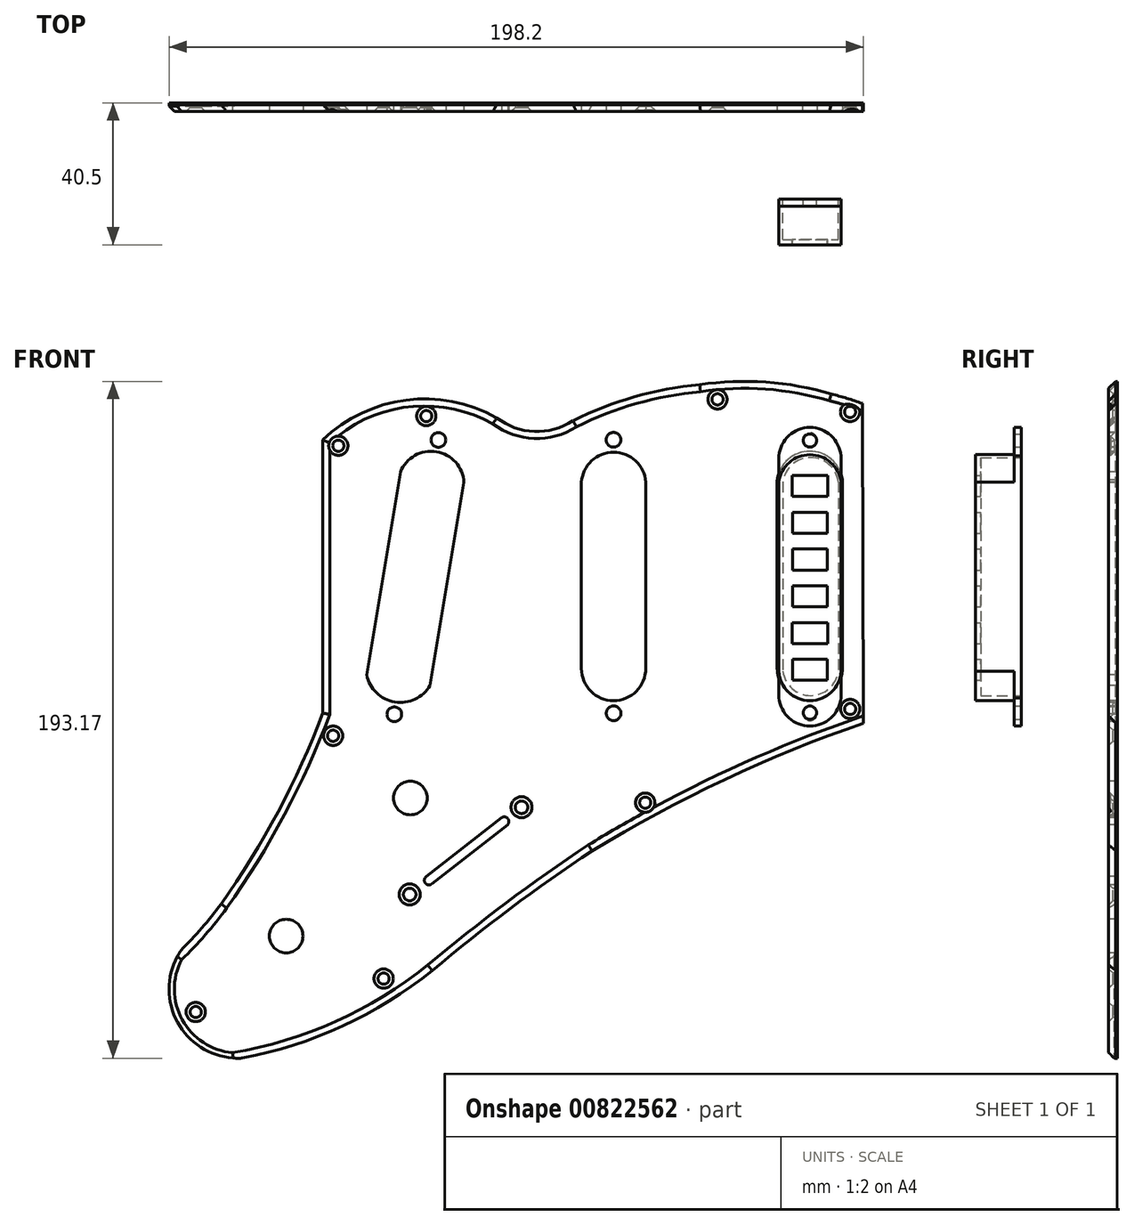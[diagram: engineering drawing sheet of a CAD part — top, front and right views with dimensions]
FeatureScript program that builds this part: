
annotation { "Feature Type Name" : "Feature", "Feature Type Description" : "" }
export const myFeature = defineFeature(function(context is Context, id is Id, definition is map)
    precondition{}
    {
        {
            var Q0;
            Q0=qCreatedBy(makeId("Front.planeOp"),FACE);
            var sketch = newSketch(context, id + "F0", { "sketchPlane" : qUnion([Q0])});
            skLineSegment(sketch, "E0", {"start": v(-59.34, 29.83) * mm, "end": v(-68.97, -28.02) * mm});
            skLineSegment(sketch, "E1", {"start": v(-41.2, 26.83) * mm, "end": v(-50.86, -31.04) * mm});
            skArc(sketch, "E2", {"start": v(-41.2, 26.83) * mm, "mid": v(-49.06, 35.63) * mm, "end": v(-59.34, 29.83) * mm});
            skArc(sketch, "E3", {"start": v(-68.97, -28.02) * mm, "mid": v(-60.95, -35.78) * mm, "end": v(-50.86, -31.04) * mm});
            skLineSegment(sketch, "E4", {"start": v(-7.67, 26.91) * mm, "end": v(-7.67, -26.25) * mm});
            skLineSegment(sketch, "E5", {"start": v(10.69, 26.94) * mm, "end": v(10.69, -26.24) * mm});
            skArc(sketch, "E6", {"start": v(10.69, 26.94) * mm, "mid": v(1.5, 35.5) * mm, "end": v(-7.67, 26.91) * mm});
            skArc(sketch, "E7", {"start": v(-7.67, -26.25) * mm, "mid": v(1.52, -35.42) * mm, "end": v(10.69, -26.24) * mm});
            skLineSegment(sketch, "E8", {"start": v(48.21, 27.6) * mm, "end": v(48.21, -26.25) * mm});
            skLineSegment(sketch, "E9", {"start": v(66.82, 27.62) * mm, "end": v(66.82, -26.21) * mm});
            skArc(sketch, "E10", {"start": v(66.82, 27.62) * mm, "mid": v(57.5, 35.79) * mm, "end": v(48.21, 27.6) * mm});
            skArc(sketch, "E11", {"start": v(48.21, -26.25) * mm, "mid": v(57.54, -35.51) * mm, "end": v(66.82, -26.21) * mm});
            skLineSegment(sketch, "E12", {"start": v(-81.5, 39) * mm, "end": v(-81.5, -38.96) * mm});
            skPoint(sketch, "E13", {"position": v(-31.85, 45.3) * mm});
            skPoint(sketch, "E14", {"position": v(-10.07, 44.47) * mm});
            skArc(sketch, "E15", {"start": v(-31.85, 45.3) * mm, "mid": v(-57.72, 50.37) * mm, "end": v(-81.5, 39) * mm});
            skArc(sketch, "E16", {"start": v(-31.85, 45.3) * mm, "mid": v(-21.1, 41.42) * mm, "end": v(-10.07, 44.47) * mm});
            skLineSegment(sketch, "E17", {"start": v(-81.5, 0) * mm, "end": v(-157.06, 0) * mm, "construction": true});
            skPoint(sketch, "E17.startSnap0", {"position": v(-81.5, 0.02) * mm});
            skLineSegment(sketch, "E18", {"start": v(-81.5, 0) * mm, "end": v(-144.5, 0) * mm, "construction": true});
            skLineSegment(sketch, "E19", {"start": v(-144.5, 0) * mm, "end": v(-144.5, -173.82) * mm, "construction": true});
            skLineSegment(sketch, "E20", {"start": v(-60.95, -39) * mm, "end": v(-60.95, -151.87) * mm, "construction": true});
            skPoint(sketch, "E20.startSnap0", {"position": v(-60.95, -35.78) * mm});
            skLineSegment(sketch, "E21", {"start": v(-60.95, -39) * mm, "end": v(-60.95, -133) * mm, "construction": true});
            skLineSegment(sketch, "E22", {"start": v(-60.95, -133) * mm, "end": v(-144.5, -133) * mm, "construction": true});
            skLineSegment(sketch, "E23", {"start": v(-60.95, -39) * mm, "end": v(-60.95, -120) * mm, "construction": true});
            skLineSegment(sketch, "E24", {"start": v(1.52, -39.01) * mm, "end": v(1.52, -84.86) * mm, "construction": true});
            skPoint(sketch, "E24.startSnap0", {"position": v(1.52, -35.42) * mm});
            skArc(sketch, "E25", {"start": v(72.84, -41.86) * mm, "mid": v(33.11, -57.95) * mm, "end": v(-4.63, -78.27) * mm});
            skLineSegment(sketch, "E26", {"start": v(-144.5, -120.92) * mm, "end": v(-81.56, -44.3) * mm, "construction": true});
            skArc(sketch, "E27", {"start": v(-4.63, -78.27) * mm, "mid": v(-27.92, -94.7) * mm, "end": v(-50.26, -112.42) * mm});
            skPoint(sketch, "E28", {"position": v(57.54, -39.01) * mm});
            skPoint(sketch, "E28.positionSnap0", {"position": v(57.54, -35.51) * mm});
            skPoint(sketch, "E29", {"position": v(57.52, 38.98) * mm});
            skPoint(sketch, "E30", {"position": v(1.5, 39.04) * mm});
            skPoint(sketch, "E31", {"position": v(-48.5, 39) * mm});
            skArc(sketch, "E32", {"start": v(72.51, 49.43) * mm, "mid": v(68.1, 50.89) * mm, "end": v(63.62, 52.12) * mm});
            skPoint(sketch, "E33.orphan", {"position": v(36.12, 48.4) * mm});
            skArc(sketch, "E34", {"start": v(26.07, 54.77) * mm, "mid": v(7.52, 51.3) * mm, "end": v(-10.07, 44.47) * mm});
            skPoint(sketch, "E34.startSnap0", {"position": v(38.43, 54.8) * mm});
            skArc(sketch, "E35", {"start": v(63.62, 52.12) * mm, "mid": v(45, 55.5) * mm, "end": v(26.07, 54.77) * mm});
            skPoint(sketch, "E36.orphan", {"position": v(44.43, 54.8) * mm});
            skPoint(sketch, "E37.center.orphan", {"position": v(-117.3, -126.97) * mm});
            skPoint(sketch, "E38.orphan", {"position": v(-117.3, -133) * mm});
            skLineSegment(sketch, "E39", {"start": v(72.51, 49.43) * mm, "end": v(72.84, -41.86) * mm});
            skPoint(sketch, "E40.center.orphan", {"position": v(72.84, 39.25) * mm});
            skPoint(sketch, "E41.endSnap0", {"position": v(-102.73, -133) * mm});
            skPoint(sketch, "E42.orphan", {"position": v(-102.73, -132.29) * mm});
            skArc(sketch, "E43", {"start": v(-110.53, -93.4) * mm, "mid": v(-94.27, -67.11) * mm, "end": v(-81.5, -38.96) * mm});
            skArc(sketch, "E44", {"start": v(-121.98, -106.7) * mm, "mid": v(-116, -100.28) * mm, "end": v(-110.53, -93.4) * mm});
            skArc(sketch, "E45.trimOffspring", {"start": v(-121.98, -106.7) * mm, "mid": v(-122.77, -127.52) * mm, "end": v(-104.44, -137.41) * mm});
            skArc(sketch, "E46", {"start": v(-104.44, -137.41) * mm, "mid": v(-75.8, -128.26) * mm, "end": v(-50.26, -112.42) * mm});
            skSolve(sketch);
        }
        {
            var Q0;
            Q0=makeQuery(id+"F0.imprint","IMPRINT",FACE,{"disambiguationData":[TD([[makeQuery(id+"F0.imprint","IMPRINT",EDGE,{"derivedFrom":sQuery(id+"F0.wireOp",EDGE,"E0")}),-1.0]])]});
            extrude(context, id + "F1", {"entities" : qUnion([Q0]), "oppositeDirection" : true, "depth" : 2.5 * mm, "offsetDistance" : 25 * mm});
        }
        {
            var Q0;
            Q0=qCreatedBy(makeId("Front.planeOp"),FACE);
            var sketch = newSketch(context, id + "F2", { "sketchPlane" : qUnion([Q0])});
            skLineSegment(sketch, "E47", {"start": v(-61.06, -39.3) * mm, "end": v(-61.06, -69.3) * mm, "construction": true});
            skPoint(sketch, "E48", {"position": v(-25.45, -64.9) * mm});
            skLineSegment(sketch, "E49", {"start": v(-29.58, -68.14) * mm, "end": v(-52.08, -85.73) * mm, "construction": true});
            skLineSegment(sketch, "E50", {"start": v(-41.4, -77.38) * mm, "end": v(-39.8, -79.43) * mm, "construction": true});
            skLineSegment(sketch, "E51", {"start": v(-41.4, -77.38) * mm, "end": v(-29.58, -68.14) * mm, "construction": true});
            skLineSegment(sketch, "E52", {"start": v(-39.8, -79.43) * mm, "end": v(-28.73, -70.77) * mm});
            skLineSegment(sketch, "E53", {"start": v(-39.8, -79.43) * mm, "end": v(-50.4, -87.72) * mm});
            skLineSegment(sketch, "E54", {"start": v(-41.4, -77.38) * mm, "end": v(-43, -75.33) * mm, "construction": true});
            skArc(sketch, "E55", {"start": v(-28.73, -70.77) * mm, "mid": v(-28.69, -69.04) * mm, "end": v(-30.4, -68.78) * mm});
            skArc(sketch, "E56", {"start": v(-51.92, -85.6) * mm, "mid": v(-52.26, -87.45) * mm, "end": v(-50.4, -87.72) * mm});
            skLineSegment(sketch, "E57", {"start": v(-51.92, -85.6) * mm, "end": v(-30.4, -68.78) * mm});
            skPoint(sketch, "E58", {"position": v(-57.35, -89.85) * mm});
            skPoint(sketch, "E59.end.orphan", {"position": v(0, -69.3) * mm});
            skPoint(sketch, "E60", {"position": v(-24.76, -65.83) * mm});
            skPoint(sketch, "E61", {"position": v(-56.69, -90.72) * mm});
            skSolve(sketch);
        }
        {
            var Q0;
            Q0=makeQuery(id+"F2.imprint","IMPRINT",FACE,{"disambiguationData":[TD([[makeQuery(id+"F2.imprint","IMPRINT",EDGE,{"derivedFrom":sQuery(id+"F2.wireOp",EDGE,"E52")}),1.0]])]});
            extrude(context, id + "F3", {"entities" : qUnion([Q0]), "operationType" : NewBodyOperationType.REMOVE, "oppositeDirection" : true, "depth" : 25 * mm, "offsetDistance" : 25 * mm});
        }
        {
            var Q0;
            Q0=qCreatedBy(makeId("Front.planeOp"),FACE);
            var sketch = newSketch(context, id + "F4", { "sketchPlane" : qUnion([Q0])});
            skLineSegment(sketch, "E62", {"start": v(-56.5, -39.58) * mm, "end": v(-56.5, -63.18) * mm, "construction": true});
            skLineSegment(sketch, "E63", {"start": v(-56.5, -63.18) * mm, "end": v(-91.93, -102.6) * mm, "construction": true});
            skSolve(sketch);
        }
        {
            var Q0;
            Q0=makeQuery(id+"F1.opExtrude","CAP_EDGE",EDGE,{"disambiguationData":[OSD([sQuery(id+"F0.wireOp",EDGE,"E27")])],"isStart":true});
            var Q1;
            Q1=makeQuery(id+"F1.opExtrude","CAP_EDGE",EDGE,{"disambiguationData":[OSD([sQuery(id+"F0.wireOp",EDGE,"3f65a524-5e08-4ee6-b38e-8508104c908b")])],"isStart":true});
            var Q2;
            Q2=makeQuery(id+"F1.opExtrude","CAP_EDGE",EDGE,{"disambiguationData":[OSD([sQuery(id+"F0.wireOp",EDGE,"6fd70a0b-cebc-4114-900a-990a1ef0163f")])],"isStart":true});
            var Q3;
            Q3=makeQuery(id+"F1.opExtrude","CAP_EDGE",EDGE,{"disambiguationData":[OSD([sQuery(id+"F0.wireOp",EDGE,"E37")])],"isStart":true});
            var Q4;
            Q4=makeQuery(id+"F1.opExtrude","CAP_EDGE",EDGE,{"disambiguationData":[OSD([sQuery(id+"F0.wireOp",EDGE,"2909704d-9c86-453f-addf-d0fc15c74224")])],"isStart":true});
            var Q5;
            Q5=makeQuery(id+"F1.opExtrude","CAP_EDGE",EDGE,{"disambiguationData":[OSD([sQuery(id+"F0.wireOp",EDGE,"E12")])],"isStart":true});
            var Q6;
            Q6=makeQuery(id+"F1.opExtrude","CAP_EDGE",EDGE,{"disambiguationData":[OSD([sQuery(id+"F0.wireOp",EDGE,"E16")])],"isStart":true});
            var Q7;
            Q7=makeQuery(id+"F1.opExtrude","CAP_EDGE",EDGE,{"disambiguationData":[OSD([sQuery(id+"F0.wireOp",EDGE,"3eeeb8b3-c194-4a8c-ba39-98cc53ac4797")])],"isStart":true});
            var Q8;
            Q8=makeQuery(id+"F1.opExtrude","CAP_EDGE",EDGE,{"disambiguationData":[OSD([sQuery(id+"F0.wireOp",EDGE,"E15")])],"isStart":true});
            var Q9;
            Q9=makeQuery(id+"F1.opExtrude","CAP_EDGE",EDGE,{"disambiguationData":[OSD([sQuery(id+"F0.wireOp",EDGE,"koqNDL3g-AHsU-HZZl-Ag6O-zdApHysT2NHa")])],"isStart":true});
            chamfer(context, id + "F5", {"entities" : qUnion([Q0, Q1, Q2, Q3, Q4, Q5, Q6, Q7, Q8, Q9]), "width" : 2 * mm, "tangentPropagation" : true});
        }
        {
            var Q0;
            Q0=qCreatedBy(makeId("Front.planeOp"),FACE);
            var sketch = newSketch(context, id + "F6", { "sketchPlane" : qUnion([Q0])});
            skPoint(sketch, "E64", {"position": v(-117.76, -124.26) * mm});
            skPoint(sketch, "E65", {"position": v(-78.53, -45.43) * mm});
            skPoint(sketch, "E66", {"position": v(-77.05, 37.34) * mm});
            skPoint(sketch, "E67", {"position": v(-51.95, 45.82) * mm});
            skPoint(sketch, "E68", {"position": v(31.17, 50.59) * mm});
            skPoint(sketch, "E69", {"position": v(69, 47) * mm});
            skPoint(sketch, "E70", {"position": v(69.05, -37.78) * mm});
            skPoint(sketch, "E71", {"position": v(10.55, -64.5) * mm});
            skPoint(sketch, "E72", {"position": v(-64.12, -114.73) * mm});
            skSolve(sketch);
        }
        {
            var Q0;
            Q0=sQuery(id+"F6.wireOp",VERTEX,"E71");
            var Q1;
            Q1=sQuery(id+"F6.wireOp",VERTEX,"E72");
            var Q2;
            Q2=sQuery(id+"F6.wireOp",VERTEX,"E64");
            var Q3;
            Q3=sQuery(id+"F6.wireOp",VERTEX,"E65");
            var Q4;
            Q4=sQuery(id+"F6.wireOp",VERTEX,"E66");
            var Q5;
            Q5=sQuery(id+"F6.wireOp",VERTEX,"E67");
            var Q6;
            Q6=sQuery(id+"F6.wireOp",VERTEX,"E68");
            var Q7;
            Q7=sQuery(id+"F6.wireOp",VERTEX,"E69");
            var Q8;
            Q8=sQuery(id+"F6.wireOp",VERTEX,"E70");
            var Q9;
            Q9=makeQuery(id+"F1.opExtrude","SWEPT_BODY",BODY,{"disambiguationData":[OSD([sQuery(id+"F0.wireOp",EDGE,"E0"),sQuery(id+"F0.wireOp",EDGE,"E1"),sQuery(id+"F0.wireOp",EDGE,"E2"),sQuery(id+"F0.wireOp",EDGE,"E3"),sQuery(id+"F0.wireOp",EDGE,"E4"),sQuery(id+"F0.wireOp",EDGE,"E5"),sQuery(id+"F0.wireOp",EDGE,"E6"),sQuery(id+"F0.wireOp",EDGE,"E7"),sQuery(id+"F0.wireOp",EDGE,"E8"),sQuery(id+"F0.wireOp",EDGE,"E9"),sQuery(id+"F0.wireOp",EDGE,"E10"),sQuery(id+"F0.wireOp",EDGE,"E11"),sQuery(id+"F0.wireOp",EDGE,"koqNDL3g-AHsU-HZZl-Ag6O-zdApHysT2NHa"),sQuery(id+"F0.wireOp",EDGE,"E12"),sQuery(id+"F0.wireOp",EDGE,"E15"),sQuery(id+"F0.wireOp",EDGE,"E16"),sQuery(id+"F0.wireOp",EDGE,"E25"),sQuery(id+"F0.wireOp",EDGE,"3fe2ab2b-aacb-4e63-9eb7-1bc754686569"),sQuery(id+"F0.wireOp",EDGE,"f01a2bd6-90c1-44fe-a7d6-a2590aa5c957"),sQuery(id+"F0.wireOp",EDGE,"2909704d-9c86-453f-addf-d0fc15c74224"),sQuery(id+"F0.wireOp",EDGE,"f144291c-5619-4e9a-93d4-3f40a0fd218b"),sQuery(id+"F0.wireOp",EDGE,"70563ed8-7092-4398-9e84-4648c7382dca"),sQuery(id+"F0.wireOp",EDGE,"E37"),sQuery(id+"F0.wireOp",EDGE,"6fd70a0b-cebc-4114-900a-990a1ef0163f"),sQuery(id+"F0.wireOp",EDGE,"d2982058-42fd-47cf-819b-9cbaea635c03"),sQuery(id+"F0.wireOp",EDGE,"3eeeb8b3-c194-4a8c-ba39-98cc53ac4797"),sQuery(id+"F0.wireOp",EDGE,"3f65a524-5e08-4ee6-b38e-8508104c908b"),sQuery(id+"F0.wireOp",EDGE,"E27")])]});
            hole(context, id + "F7", {"style" : HoleStyle.C_SINK, "endStyle" : HoleEndStyle.THROUGH, "holeDiameter" : 3.2 * mm, "cSinkDiameter" : 5.5 * mm, "cSinkAngle" : 90 * degree, "majorDiameter" : 5 * mm, "isTappedThrough" : true, "tappedDepth" : 12 * mm, "tapClearance" : 3, "locations" : qUnion([Q0, Q1, Q2, Q3, Q4, Q5, Q6, Q7, Q8]), "scope" : qUnion([Q9])});
        }
        {
            var Q0;
            Q0=sQuery(id+"F0.wireOp",VERTEX,"E30");
            var Q1;
            Q1=sQuery(id+"F0.wireOp",VERTEX,"E29");
            var Q2;
            Q2=sQuery(id+"F0.wireOp",VERTEX,"E28");
            var Q3;
            Q3=sQuery(id+"F0.wireOp",VERTEX,"E24.start");
            var Q4;
            Q4=sQuery(id+"F0.wireOp",VERTEX,"E31");
            var Q5;
            Q5=sQuery(id+"F2.wireOp",VERTEX,"E47.start");
            var Q6;
            Q6=makeQuery(id+"F1.opExtrude","SWEPT_BODY",BODY,{"disambiguationData":[OSD([sQuery(id+"F0.wireOp",EDGE,"E0"),sQuery(id+"F0.wireOp",EDGE,"E1"),sQuery(id+"F0.wireOp",EDGE,"E2"),sQuery(id+"F0.wireOp",EDGE,"E3"),sQuery(id+"F0.wireOp",EDGE,"E4"),sQuery(id+"F0.wireOp",EDGE,"E5"),sQuery(id+"F0.wireOp",EDGE,"E6"),sQuery(id+"F0.wireOp",EDGE,"E7"),sQuery(id+"F0.wireOp",EDGE,"E8"),sQuery(id+"F0.wireOp",EDGE,"E9"),sQuery(id+"F0.wireOp",EDGE,"E10"),sQuery(id+"F0.wireOp",EDGE,"E11"),sQuery(id+"F0.wireOp",EDGE,"koqNDL3g-AHsU-HZZl-Ag6O-zdApHysT2NHa"),sQuery(id+"F0.wireOp",EDGE,"E12"),sQuery(id+"F0.wireOp",EDGE,"E15"),sQuery(id+"F0.wireOp",EDGE,"E16"),sQuery(id+"F0.wireOp",EDGE,"E25"),sQuery(id+"F0.wireOp",EDGE,"3fe2ab2b-aacb-4e63-9eb7-1bc754686569"),sQuery(id+"F0.wireOp",EDGE,"f01a2bd6-90c1-44fe-a7d6-a2590aa5c957"),sQuery(id+"F0.wireOp",EDGE,"2909704d-9c86-453f-addf-d0fc15c74224"),sQuery(id+"F0.wireOp",EDGE,"f144291c-5619-4e9a-93d4-3f40a0fd218b"),sQuery(id+"F0.wireOp",EDGE,"70563ed8-7092-4398-9e84-4648c7382dca"),sQuery(id+"F0.wireOp",EDGE,"E37"),sQuery(id+"F0.wireOp",EDGE,"6fd70a0b-cebc-4114-900a-990a1ef0163f"),sQuery(id+"F0.wireOp",EDGE,"d2982058-42fd-47cf-819b-9cbaea635c03"),sQuery(id+"F0.wireOp",EDGE,"3eeeb8b3-c194-4a8c-ba39-98cc53ac4797"),sQuery(id+"F0.wireOp",EDGE,"3f65a524-5e08-4ee6-b38e-8508104c908b"),sQuery(id+"F0.wireOp",EDGE,"E27")])]});
            hole(context, id + "F8", {"style" : HoleStyle.SIMPLE, "endStyle" : HoleEndStyle.THROUGH, "holeDiameter" : 4.2 * mm, "majorDiameter" : 5 * mm, "isTappedThrough" : true, "tappedDepth" : 12 * mm, "tapClearance" : 3, "locations" : qUnion([Q0, Q1, Q2, Q3, Q4, Q5]), "scope" : qUnion([Q6])});
        }
        {
            var Q0;
            Q0=qCreatedBy(makeId("Front.planeOp"),FACE);
            cPlane(context, id + "F9", {"entities" : qUnion([Q0]), "cplaneType" : CPlaneType.OFFSET, "offset" : 25 * mm, "width" : 150 * mm, "height" : 150 * mm});
        }
        {
            var Q0;
            Q0=qCreatedBy(id+"F9.planeOp",FACE);
            var sketch = newSketch(context, id + "F10", { "sketchPlane" : qUnion([Q0])});
            skLineSegment(sketch, "E73", {"start": v(57.55, 0) * mm, "end": v(66.35, 0) * mm, "construction": true});
            skLineSegment(sketch, "E74.left", {"start": v(66.4, -27) * mm, "end": v(66.4, 27) * mm});
            skLineSegment(sketch, "E74.right", {"start": v(48.7, -27) * mm, "end": v(48.7, 27) * mm});
            skPoint(sketch, "E74.middle", {"position": v(57.55, 0) * mm});
            skArc(sketch, "E75", {"start": v(66.4, 27) * mm, "mid": v(57.55, 34.8) * mm, "end": v(48.7, 27) * mm});
            skArc(sketch, "E76", {"start": v(48.7, -27) * mm, "mid": v(57.55, -35.45) * mm, "end": v(66.4, -27) * mm});
            skLineSegment(sketch, "E77", {"start": v(48.7, 27) * mm, "end": v(48.7, 34.48) * mm});
            skLineSegment(sketch, "E78", {"start": v(66.4, 27) * mm, "end": v(66.4, 34.48) * mm});
            skLineSegment(sketch, "E79", {"start": v(48.7, 37.17) * mm, "end": v(66.4, 37.17) * mm, "construction": true});
            skLineSegment(sketch, "E80", {"start": v(57.55, -38.84) * mm, "end": v(71.22, -38.84) * mm, "construction": true});
            skLineSegment(sketch, "E81", {"start": v(66.4, -27) * mm, "end": v(66.4, -34.6) * mm});
            skLineSegment(sketch, "E82", {"start": v(48.7, -27) * mm, "end": v(48.7, -34.6) * mm});
            skPoint(sketch, "E83.orphan", {"position": v(57.55, 38.84) * mm});
            skLineSegment(sketch, "E84", {"start": v(57.55, 25.87) * mm, "end": v(57.55, 15.37) * mm, "construction": true});
            skLineSegment(sketch, "E85", {"start": v(57.55, 15.37) * mm, "end": v(57.55, 4.87) * mm, "construction": true});
            skLineSegment(sketch, "E86", {"start": v(57.55, 4.87) * mm, "end": v(57.55, -5.63) * mm, "construction": true});
            skLineSegment(sketch, "E87", {"start": v(57.55, -5.63) * mm, "end": v(57.55, -16.13) * mm, "construction": true});
            skLineSegment(sketch, "E88", {"start": v(57.55, -16.13) * mm, "end": v(57.55, -26.63) * mm, "construction": true});
            skLineSegment(sketch, "E89", {"start": v(52.68, 37.17) * mm, "end": v(52.68, -31.17) * mm, "construction": true});
            skLineSegment(sketch, "E90.bottom", {"start": v(62.59, 22.87) * mm, "end": v(52.52, 22.87) * mm});
            skLineSegment(sketch, "E90.top", {"start": v(62.59, 28.87) * mm, "end": v(52.52, 28.87) * mm});
            skLineSegment(sketch, "E90.left", {"start": v(62.59, 22.87) * mm, "end": v(62.59, 28.87) * mm});
            skLineSegment(sketch, "E90.right", {"start": v(52.52, 22.87) * mm, "end": v(52.52, 28.87) * mm});
            skLineSegment(sketch, "E91.bottom", {"start": v(62.54, 12.37) * mm, "end": v(52.56, 12.37) * mm});
            skLineSegment(sketch, "E91.top", {"start": v(62.54, 18.37) * mm, "end": v(52.56, 18.37) * mm});
            skLineSegment(sketch, "E91.left", {"start": v(62.54, 12.37) * mm, "end": v(62.54, 18.37) * mm});
            skLineSegment(sketch, "E91.right", {"start": v(52.56, 12.37) * mm, "end": v(52.56, 18.37) * mm});
            skPoint(sketch, "E91.middle", {"position": v(57.55, 15.37) * mm});
            skLineSegment(sketch, "E92.bottom", {"start": v(62.48, 1.87) * mm, "end": v(52.63, 1.87) * mm});
            skLineSegment(sketch, "E92.top", {"start": v(62.48, 7.87) * mm, "end": v(52.63, 7.87) * mm});
            skLineSegment(sketch, "E92.left", {"start": v(62.48, 1.87) * mm, "end": v(62.48, 7.87) * mm});
            skLineSegment(sketch, "E92.right", {"start": v(52.63, 1.87) * mm, "end": v(52.63, 7.87) * mm});
            skPoint(sketch, "E92.middle", {"position": v(57.55, 4.87) * mm});
            skLineSegment(sketch, "E93.bottom", {"start": v(62.56, -8.63) * mm, "end": v(52.55, -8.63) * mm});
            skLineSegment(sketch, "E93.top", {"start": v(62.56, -2.63) * mm, "end": v(52.55, -2.63) * mm});
            skLineSegment(sketch, "E93.left", {"start": v(62.56, -8.63) * mm, "end": v(62.56, -2.63) * mm});
            skLineSegment(sketch, "E93.right", {"start": v(52.55, -8.63) * mm, "end": v(52.55, -2.63) * mm});
            skPoint(sketch, "E93.middle", {"position": v(57.55, -5.63) * mm});
            skLineSegment(sketch, "E94.bottom", {"start": v(62.68, -19.13) * mm, "end": v(52.43, -19.13) * mm});
            skLineSegment(sketch, "E94.top", {"start": v(62.68, -13.13) * mm, "end": v(52.43, -13.13) * mm});
            skLineSegment(sketch, "E94.left", {"start": v(62.68, -19.13) * mm, "end": v(62.68, -13.13) * mm});
            skLineSegment(sketch, "E94.right", {"start": v(52.43, -19.13) * mm, "end": v(52.43, -13.13) * mm});
            skPoint(sketch, "E94.middle", {"position": v(57.55, -16.13) * mm});
            skLineSegment(sketch, "E95.bottom", {"start": v(62.54, -29.59) * mm, "end": v(52.56, -29.59) * mm});
            skLineSegment(sketch, "E95.top", {"start": v(62.54, -23.59) * mm, "end": v(52.56, -23.59) * mm});
            skLineSegment(sketch, "E95.left", {"start": v(62.54, -29.59) * mm, "end": v(62.54, -23.59) * mm});
            skLineSegment(sketch, "E95.right", {"start": v(52.56, -29.59) * mm, "end": v(52.56, -23.59) * mm});
            skArc(sketch, "E96", {"start": v(66.4, 32.9) * mm, "mid": v(57.55, 42.57) * mm, "end": v(48.7, 32.9) * mm});
            skPoint(sketch, "E96.startSnap0", {"position": v(48.7, 32.9) * mm});
            skPoint(sketch, "E97.orphan", {"position": v(66.4, 38.78) * mm});
            skPoint(sketch, "E98.orphan", {"position": v(48.7, 38.78) * mm});
            skArc(sketch, "E99", {"start": v(48.7, -34.6) * mm, "mid": v(57.55, -42.65) * mm, "end": v(66.4, -34.6) * mm});
            skPoint(sketch, "E100.orphan", {"position": v(48.7, -38.84) * mm});
            skPoint(sketch, "E101.orphan", {"position": v(48.7, -32.92) * mm});
            skPoint(sketch, "E102.orphan", {"position": v(66.4, -38.84) * mm});
            skPoint(sketch, "E103.orphan", {"position": v(66.4, -32.92) * mm});
            skSolve(sketch);
        }
        {
            var Q0;
            Q0=makeQuery(id+"F10.imprint","IMPRINT",FACE,{"disambiguationData":[TD([[makeQuery(id+"F10.imprint","IMPRINT",EDGE,{"derivedFrom":sQuery(id+"F10.wireOp",EDGE,"E74.left")}),1.0]])]});
            extrude(context, id + "F11", {"entities" : qUnion([Q0]), "depth" : 13 * mm, "offsetDistance" : 25 * mm});
        }
        {
            var Q0;
            Q0=makeQuery(id+"F10.imprint","IMPRINT",FACE,{"disambiguationData":[TD([[makeQuery(id+"F10.imprint","IMPRINT",EDGE,{"derivedFrom":sQuery(id+"F10.wireOp",EDGE,"E76")}),-1.0]])]});
            var Q1;
            {var subQ1=sQuery(id+"F10.wireOp",EDGE,"E75");Q1=makeQuery(id+"F10.imprint","IMPRINT",FACE,{"disambiguationData":[TD([[makeQuery(id+"F10.imprint","IMPRINT",EDGE,{"derivedFrom":subQ1}),-1.0]])]});}
            extrude(context, id + "F12", {"entities" : qUnion([Q0, Q1]), "operationType" : NewBodyOperationType.ADD, "depth" : 2 * mm, "offsetDistance" : 25 * mm});
        }
        {
            var Q0;
            Q0=qCreatedBy(id+"F9.planeOp",FACE);
            var sketch = newSketch(context, id + "F13", { "sketchPlane" : qUnion([Q0])});
            skLineSegment(sketch, "E104", {"start": v(65.69, 26.99) * mm, "end": v(65.69, -26.99) * mm});
            skLineSegment(sketch, "E105", {"start": v(49.83, 26.98) * mm, "end": v(49.83, -26.99) * mm});
            skArc(sketch, "E106", {"start": v(49.83, -26.99) * mm, "mid": v(57.76, -33.95) * mm, "end": v(65.69, -26.99) * mm});
            skLineSegment(sketch, "E107", {"start": v(65.69, -19.5) * mm, "end": v(49.83, -19.5) * mm, "construction": true});
            skPoint(sketch, "E108.orphan", {"position": v(66.05, -26.99) * mm});
            skPoint(sketch, "E109.end.orphan", {"position": v(66.4, 0) * mm});
            skPoint(sketch, "E109.start.orphan", {"position": v(66.05, 0) * mm});
            skArc(sketch, "E110", {"start": v(65.69, 26.99) * mm, "mid": v(57.76, 33.96) * mm, "end": v(49.83, 26.98) * mm});
            skPoint(sketch, "E111.end.orphan", {"position": v(49.17, 26.98) * mm});
            skPoint(sketch, "E111.start.orphan", {"position": v(66.05, 26.98) * mm});
            skSolve(sketch);
        }
        {
            var Q0;
            Q0=makeQuery(id+"F13.imprint","IMPRINT",FACE,{"disambiguationData":[TD([[makeQuery(id+"F13.imprint","IMPRINT",EDGE,{"derivedFrom":sQuery(id+"F13.wireOp",EDGE,"E104")}),-1.0]])]});
            extrude(context, id + "F14", {"entities" : qUnion([Q0]), "operationType" : NewBodyOperationType.REMOVE, "depth" : 11.5 * mm, "offsetDistance" : 25 * mm});
        }
        {
            var Q0;
            Q0=sQuery(id+"F10.wireOp",VERTEX,"E80.start");
            var Q1;
            Q1=sQuery(id+"F10.wireOp",VERTEX,"E83.orphan");
            var Q2;
            Q2=makeQuery(id+"F11.opExtrude","SWEPT_BODY",BODY,{"disambiguationData":[OSD([sQuery(id+"F10.wireOp",EDGE,"E74.left"),sQuery(id+"F10.wireOp",EDGE,"E74.right"),sQuery(id+"F10.wireOp",EDGE,"E75"),sQuery(id+"F10.wireOp",EDGE,"E76"),sQuery(id+"F10.wireOp",EDGE,"E90.bottom"),sQuery(id+"F10.wireOp",EDGE,"E90.top"),sQuery(id+"F10.wireOp",EDGE,"E90.left"),sQuery(id+"F10.wireOp",EDGE,"E90.right"),sQuery(id+"F10.wireOp",EDGE,"E91.bottom"),sQuery(id+"F10.wireOp",EDGE,"E91.top"),sQuery(id+"F10.wireOp",EDGE,"E91.left"),sQuery(id+"F10.wireOp",EDGE,"E91.right"),sQuery(id+"F10.wireOp",EDGE,"E92.bottom"),sQuery(id+"F10.wireOp",EDGE,"E92.top"),sQuery(id+"F10.wireOp",EDGE,"E92.left"),sQuery(id+"F10.wireOp",EDGE,"E92.right"),sQuery(id+"F10.wireOp",EDGE,"E93.bottom"),sQuery(id+"F10.wireOp",EDGE,"E93.top"),sQuery(id+"F10.wireOp",EDGE,"E93.left"),sQuery(id+"F10.wireOp",EDGE,"E93.right"),sQuery(id+"F10.wireOp",EDGE,"E94.bottom"),sQuery(id+"F10.wireOp",EDGE,"E94.top"),sQuery(id+"F10.wireOp",EDGE,"E94.left"),sQuery(id+"F10.wireOp",EDGE,"E94.right"),sQuery(id+"F10.wireOp",EDGE,"E95.bottom"),sQuery(id+"F10.wireOp",EDGE,"E95.top"),sQuery(id+"F10.wireOp",EDGE,"E95.left"),sQuery(id+"F10.wireOp",EDGE,"E95.right")])]});
            hole(context, id + "F15", {"style" : HoleStyle.SIMPLE, "endStyle" : HoleEndStyle.THROUGH, "oppositeDirection" : true, "holeDiameter" : 3.8 * mm, "majorDiameter" : 5 * mm, "isTappedThrough" : true, "tappedDepth" : 12 * mm, "tapClearance" : 3, "locations" : qUnion([Q0, Q1]), "scope" : qUnion([Q2])});
        }
        {
            var Q0;
            Q0=sQuery(id+"F2.wireOp",VERTEX,"E60");
            var Q1;
            Q1=sQuery(id+"F2.wireOp",VERTEX,"E61");
            var Q2;
            Q2=makeQuery(id+"F1.opExtrude","SWEPT_BODY",BODY,{"disambiguationData":[OSD([sQuery(id+"F0.wireOp",EDGE,"E0"),sQuery(id+"F0.wireOp",EDGE,"E1"),sQuery(id+"F0.wireOp",EDGE,"E2"),sQuery(id+"F0.wireOp",EDGE,"E3"),sQuery(id+"F0.wireOp",EDGE,"E4"),sQuery(id+"F0.wireOp",EDGE,"E5"),sQuery(id+"F0.wireOp",EDGE,"E6"),sQuery(id+"F0.wireOp",EDGE,"E7"),sQuery(id+"F0.wireOp",EDGE,"E8"),sQuery(id+"F0.wireOp",EDGE,"E9"),sQuery(id+"F0.wireOp",EDGE,"E10"),sQuery(id+"F0.wireOp",EDGE,"E11"),sQuery(id+"F0.wireOp",EDGE,"koqNDL3g-AHsU-HZZl-Ag6O-zdApHysT2NHa"),sQuery(id+"F0.wireOp",EDGE,"E12"),sQuery(id+"F0.wireOp",EDGE,"E15"),sQuery(id+"F0.wireOp",EDGE,"E16"),sQuery(id+"F0.wireOp",EDGE,"E25"),sQuery(id+"F0.wireOp",EDGE,"3fe2ab2b-aacb-4e63-9eb7-1bc754686569"),sQuery(id+"F0.wireOp",EDGE,"f01a2bd6-90c1-44fe-a7d6-a2590aa5c957"),sQuery(id+"F0.wireOp",EDGE,"2909704d-9c86-453f-addf-d0fc15c74224"),sQuery(id+"F0.wireOp",EDGE,"f144291c-5619-4e9a-93d4-3f40a0fd218b"),sQuery(id+"F0.wireOp",EDGE,"70563ed8-7092-4398-9e84-4648c7382dca"),sQuery(id+"F0.wireOp",EDGE,"E37"),sQuery(id+"F0.wireOp",EDGE,"6fd70a0b-cebc-4114-900a-990a1ef0163f"),sQuery(id+"F0.wireOp",EDGE,"d2982058-42fd-47cf-819b-9cbaea635c03"),sQuery(id+"F0.wireOp",EDGE,"3eeeb8b3-c194-4a8c-ba39-98cc53ac4797"),sQuery(id+"F0.wireOp",EDGE,"3f65a524-5e08-4ee6-b38e-8508104c908b"),sQuery(id+"F0.wireOp",EDGE,"E27")])]});
            hole(context, id + "F16", {"style" : HoleStyle.C_SINK, "endStyle" : HoleEndStyle.THROUGH, "holeDiameter" : 3.6 * mm, "cSinkDiameter" : 6 * mm, "cSinkAngle" : 90 * degree, "majorDiameter" : 5 * mm, "isTappedThrough" : true, "tappedDepth" : 12 * mm, "tapClearance" : 3, "locations" : qUnion([Q0, Q1]), "scope" : qUnion([Q2])});
        }
        {
            var Q0;
            Q0=sQuery(id+"F4.wireOp",VERTEX,"E62.end");
            var Q1;
            Q1=sQuery(id+"F4.wireOp",VERTEX,"E63.end");
            var Q2;
            Q2=makeQuery(id+"F1.opExtrude","SWEPT_BODY",BODY,{"disambiguationData":[OSD([sQuery(id+"F0.wireOp",EDGE,"E0"),sQuery(id+"F0.wireOp",EDGE,"E1"),sQuery(id+"F0.wireOp",EDGE,"E2"),sQuery(id+"F0.wireOp",EDGE,"E3"),sQuery(id+"F0.wireOp",EDGE,"E4"),sQuery(id+"F0.wireOp",EDGE,"E5"),sQuery(id+"F0.wireOp",EDGE,"E6"),sQuery(id+"F0.wireOp",EDGE,"E7"),sQuery(id+"F0.wireOp",EDGE,"E8"),sQuery(id+"F0.wireOp",EDGE,"E9"),sQuery(id+"F0.wireOp",EDGE,"E10"),sQuery(id+"F0.wireOp",EDGE,"E11"),sQuery(id+"F0.wireOp",EDGE,"koqNDL3g-AHsU-HZZl-Ag6O-zdApHysT2NHa"),sQuery(id+"F0.wireOp",EDGE,"E12"),sQuery(id+"F0.wireOp",EDGE,"E15"),sQuery(id+"F0.wireOp",EDGE,"E16"),sQuery(id+"F0.wireOp",EDGE,"E25"),sQuery(id+"F0.wireOp",EDGE,"3fe2ab2b-aacb-4e63-9eb7-1bc754686569"),sQuery(id+"F0.wireOp",EDGE,"f01a2bd6-90c1-44fe-a7d6-a2590aa5c957"),sQuery(id+"F0.wireOp",EDGE,"2909704d-9c86-453f-addf-d0fc15c74224"),sQuery(id+"F0.wireOp",EDGE,"f144291c-5619-4e9a-93d4-3f40a0fd218b"),sQuery(id+"F0.wireOp",EDGE,"70563ed8-7092-4398-9e84-4648c7382dca"),sQuery(id+"F0.wireOp",EDGE,"E37"),sQuery(id+"F0.wireOp",EDGE,"6fd70a0b-cebc-4114-900a-990a1ef0163f"),sQuery(id+"F0.wireOp",EDGE,"d2982058-42fd-47cf-819b-9cbaea635c03"),sQuery(id+"F0.wireOp",EDGE,"3eeeb8b3-c194-4a8c-ba39-98cc53ac4797"),sQuery(id+"F0.wireOp",EDGE,"3f65a524-5e08-4ee6-b38e-8508104c908b"),sQuery(id+"F0.wireOp",EDGE,"E27")])]});
            hole(context, id + "F17", {"style" : HoleStyle.SIMPLE, "endStyle" : HoleEndStyle.THROUGH, "holeDiameter" : 9.6 * mm, "majorDiameter" : 5 * mm, "isTappedThrough" : true, "tappedDepth" : 12 * mm, "tapClearance" : 3, "locations" : qUnion([Q0, Q1]), "scope" : qUnion([Q2])});
        }
        {
            var Q0;
            Q0=makeQuery(id+"F1.opExtrude","CAP_EDGE",EDGE,{"disambiguationData":[OSD([sQuery(id+"F0.wireOp",EDGE,"E46")])],"isStart":true});
            var Q1;
            Q1=makeQuery(id+"F1.opExtrude","CAP_EDGE",EDGE,{"disambiguationData":[OSD([sQuery(id+"F0.wireOp",EDGE,"E43")])],"isStart":true});
            var Q2;
            Q2=makeQuery(id+"F1.opExtrude","CAP_EDGE",EDGE,{"disambiguationData":[OSD([sQuery(id+"F0.wireOp",EDGE,"E34")])],"isStart":true});
            var Q3;
            Q3=makeQuery(id+"F1.opExtrude","CAP_EDGE",EDGE,{"disambiguationData":[OSD([sQuery(id+"F0.wireOp",EDGE,"E35")])],"isStart":true});
            chamfer(context, id + "F18", {"entities" : qUnion([Q0, Q1, Q2, Q3]), "width" : 2 * mm, "tangentPropagation" : true});
        }
        {
            var Q0;
            Q0=makeQuery(id+"F1.opExtrude","CAP_EDGE",EDGE,{"disambiguationData":[OSD([sQuery(id+"F0.wireOp",EDGE,"E45.trimOffspring")])],"isStart":true});
            chamfer(context, id + "F19", {"entities" : qUnion([Q0]), "width" : 1.5 * mm, "tangentPropagation" : true});
        }
    });
